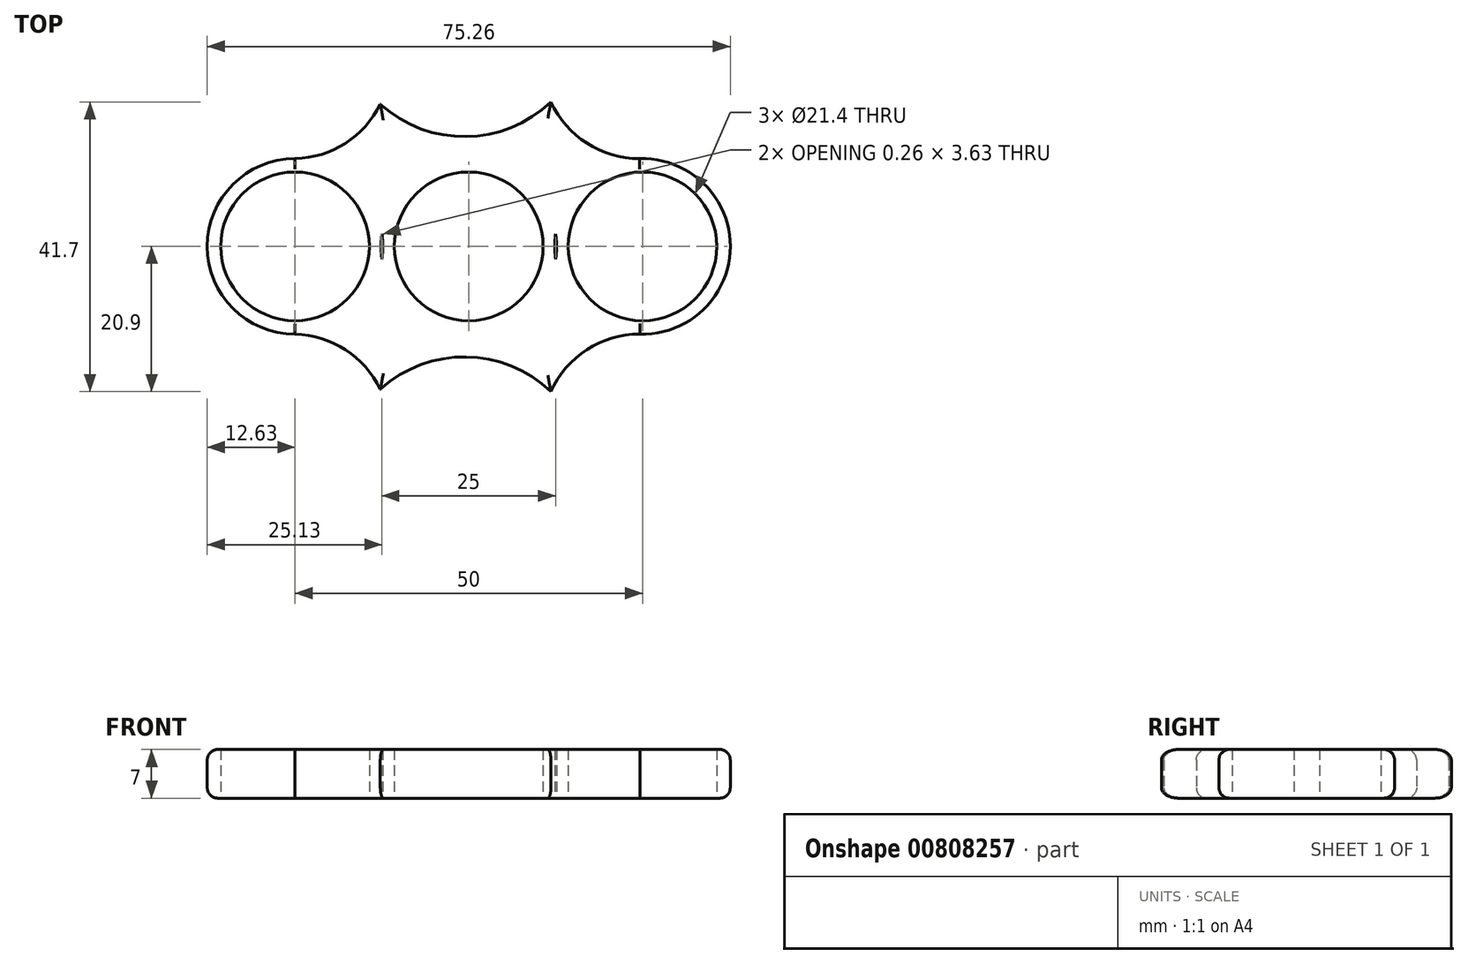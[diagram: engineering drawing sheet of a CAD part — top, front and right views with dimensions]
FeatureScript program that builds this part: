
annotation { "Feature Type Name" : "Feature", "Feature Type Description" : "" }
export const myFeature = defineFeature(function(context is Context, id is Id, definition is map)
    precondition{}
    {
        {
            var Q0;
            Q0=qCreatedBy(makeId("Top.planeOp"),FACE);
            var sketch = newSketch(context, id + "F0", { "sketchPlane" : qUnion([Q0])});
            skCircle(sketch, "E0", {"center": v(0, 0) * mm, "radius": 10.7 * mm});
            skCircle(sketch, "E1", {"center": v(0, 0) * mm, "radius": 12.63 * mm});
            skCircle(sketch, "E2.1.0.0", {"center": v(25, 0) * mm, "radius": 12.63 * mm});
            skCircle(sketch, "E2.2.0.0", {"center": v(50, 0) * mm, "radius": 12.63 * mm});
            skLineSegment(sketch, "E2.direction1", {"start": v(0, 0) * mm, "end": v(25, 0) * mm, "construction": true});
            skCircle(sketch, "E3.1.0.0", {"center": v(25, 0) * mm, "radius": 10.7 * mm});
            skCircle(sketch, "E3.2.0.0", {"center": v(50, 0) * mm, "radius": 10.7 * mm});
            skArc(sketch, "E4", {"start": v(36.82, -20.9) * mm, "mid": v(24.61, -15.9) * mm, "end": v(12.27, -20.57) * mm});
            skArc(sketch, "E5", {"start": v(12.27, 20.47) * mm, "mid": v(24.61, 15.8) * mm, "end": v(36.82, 20.8) * mm});
            skArc(sketch, "E6", {"start": v(12.27, -20.57) * mm, "mid": v(7.25, -14.87) * mm, "end": v(0, -12.63) * mm});
            skArc(sketch, "E7", {"start": v(50, -12.63) * mm, "mid": v(42.16, -14.77) * mm, "end": v(36.82, -20.9) * mm});
            skArc(sketch, "E8", {"start": v(0, 12.63) * mm, "mid": v(7.24, 14.83) * mm, "end": v(12.27, 20.47) * mm});
            skArc(sketch, "E9", {"start": v(36.82, 20.8) * mm, "mid": v(42.18, 14.73) * mm, "end": v(50, 12.63) * mm});
            skSolve(sketch);
        }
        {
            var Q0;
            Q0 = qSketchRegion(id + "F0", true);
            var Q1;
            Q1=makeQuery(id+"F0.imprint","IMPRINT",FACE,{"disambiguationData":[TD([[makeQuery(id+"F0.imprint","IMPRINT",EDGE,{"derivedFrom":sQuery(id+"F0.wireOp",EDGE,"E3.1.0.0")}),-1.0]])]});
            extrude(context, id + "F1", {"entities" : qUnion([Q0, Q1]), "depth" : 7 * mm, "offsetDistance" : 25 * mm});
        }
        {
            var Q0;
            Q0=makeQuery(id+"F1.opExtrude","CAP_EDGE",EDGE,{"disambiguationData":[OSD([sQuery(id+"F0.wireOp",EDGE,"E5")])],"isStart":false});
            var Q1;
            Q1=makeQuery(id+"F1.opExtrude","CAP_EDGE",EDGE,{"disambiguationData":[OSD([sQuery(id+"F0.wireOp",EDGE,"E8")])],"isStart":false});
            var Q2;
            {var subQ0=sQuery(id+"F0.wireOp",EDGE,"E1");Q2=makeQuery(id+"F1.opExtrude","CAP_EDGE",EDGE,{"disambiguationData":[OSD([subQ0]),TDD([makeQuery(id+"F0.imprint","IMPRINT",EDGE,{"disambiguationData":[TD([[makeQuery(id+"F0.imprint","INTERSECT",VERTEX,{"derivedFrom":[subQ0,sQuery(id+"F0.wireOp",EDGE,"E6")]}),1.0]])],"derivedFrom":subQ0})])],"isStart":false});}
            var Q3;
            Q3=makeQuery(id+"F1.opExtrude","CAP_EDGE",EDGE,{"disambiguationData":[OSD([sQuery(id+"F0.wireOp",EDGE,"E4")])],"isStart":false});
            var Q4;
            Q4=makeQuery(id+"F1.opExtrude","CAP_EDGE",EDGE,{"disambiguationData":[OSD([sQuery(id+"F0.wireOp",EDGE,"E7")])],"isStart":false});
            var Q5;
            {var subQ0=sQuery(id+"F0.wireOp",EDGE,"E7");var subQ1=sQuery(id+"F0.wireOp",EDGE,"E2.2.0.0");var subQ2=makeQuery(id+"F0.imprint","INTERSECT",VERTEX,{"disambiguationData":[OD(0.0)],"derivedFrom":[subQ1,subQ0]});var subQ3=sQuery(id+"F0.wireOp",EDGE,"E9");var subQ4=makeQuery(id+"F0.imprint","INTERSECT",VERTEX,{"disambiguationData":[OD(0.0)],"derivedFrom":[subQ1,subQ3]});Q5=makeQuery(id+"F1.opExtrude","CAP_EDGE",EDGE,{"disambiguationData":[OSD([subQ1]),TDD([makeQuery(id+"F0.imprint","IMPRINT",EDGE,{"disambiguationData":[TD([[subQ4,-1.0]])],"derivedFrom":subQ1}),makeQuery(id+"F0.imprint","IMPRINT",EDGE,{"disambiguationData":[TD([[subQ2,1.0]])],"derivedFrom":subQ1}),makeQuery(id+"F0.imprint","IMPRINT",EDGE,{"disambiguationData":[TD([[subQ2,-1.0]])],"derivedFrom":subQ1})])],"isStart":false});}
            fillet(context, id + "F2", {"entities" : qUnion([Q0, Q1, Q2, Q3, Q4, Q5]), "radius" : 1.5 * mm, "tangentPropagation" : true, "allowEdgeOverflow" : false});
        }
        {
            var Q0;
            Q0=makeQuery(id+"F1.opExtrude","CAP_EDGE",EDGE,{"disambiguationData":[OSD([sQuery(id+"F0.wireOp",EDGE,"E4")])],"isStart":true});
            var Q1;
            Q1=makeQuery(id+"F1.opExtrude","CAP_EDGE",EDGE,{"disambiguationData":[OSD([sQuery(id+"F0.wireOp",EDGE,"E6")])],"isStart":true});
            var Q2;
            {var subQ0=sQuery(id+"F0.wireOp",EDGE,"E1");Q2=makeQuery(id+"F1.opExtrude","CAP_EDGE",EDGE,{"disambiguationData":[OSD([subQ0]),TDD([makeQuery(id+"F0.imprint","IMPRINT",EDGE,{"disambiguationData":[TD([[makeQuery(id+"F0.imprint","INTERSECT",VERTEX,{"derivedFrom":[subQ0,sQuery(id+"F0.wireOp",EDGE,"E6")]}),1.0]])],"derivedFrom":subQ0})])],"isStart":true});}
            var Q3;
            Q3=makeQuery(id+"F1.opExtrude","CAP_EDGE",EDGE,{"disambiguationData":[OSD([sQuery(id+"F0.wireOp",EDGE,"E5")])],"isStart":true});
            var Q4;
            Q4=makeQuery(id+"F1.opExtrude","CAP_EDGE",EDGE,{"disambiguationData":[OSD([sQuery(id+"F0.wireOp",EDGE,"E9")])],"isStart":true});
            var Q5;
            {var subQ0=sQuery(id+"F0.wireOp",EDGE,"E7");var subQ1=sQuery(id+"F0.wireOp",EDGE,"E2.2.0.0");var subQ2=makeQuery(id+"F0.imprint","INTERSECT",VERTEX,{"disambiguationData":[OD(0.0)],"derivedFrom":[subQ1,subQ0]});var subQ3=sQuery(id+"F0.wireOp",EDGE,"E9");var subQ4=makeQuery(id+"F0.imprint","INTERSECT",VERTEX,{"disambiguationData":[OD(0.0)],"derivedFrom":[subQ1,subQ3]});Q5=makeQuery(id+"F1.opExtrude","CAP_EDGE",EDGE,{"disambiguationData":[OSD([subQ1]),TDD([makeQuery(id+"F0.imprint","IMPRINT",EDGE,{"disambiguationData":[TD([[subQ4,-1.0]])],"derivedFrom":subQ1}),makeQuery(id+"F0.imprint","IMPRINT",EDGE,{"disambiguationData":[TD([[subQ2,1.0]])],"derivedFrom":subQ1}),makeQuery(id+"F0.imprint","IMPRINT",EDGE,{"disambiguationData":[TD([[subQ2,-1.0]])],"derivedFrom":subQ1})])],"isStart":true});}
            fillet(context, id + "F3", {"entities" : qUnion([Q0, Q1, Q2, Q3, Q4, Q5]), "radius" : 1.5 * mm, "tangentPropagation" : true, "allowEdgeOverflow" : false});
        }
    });
